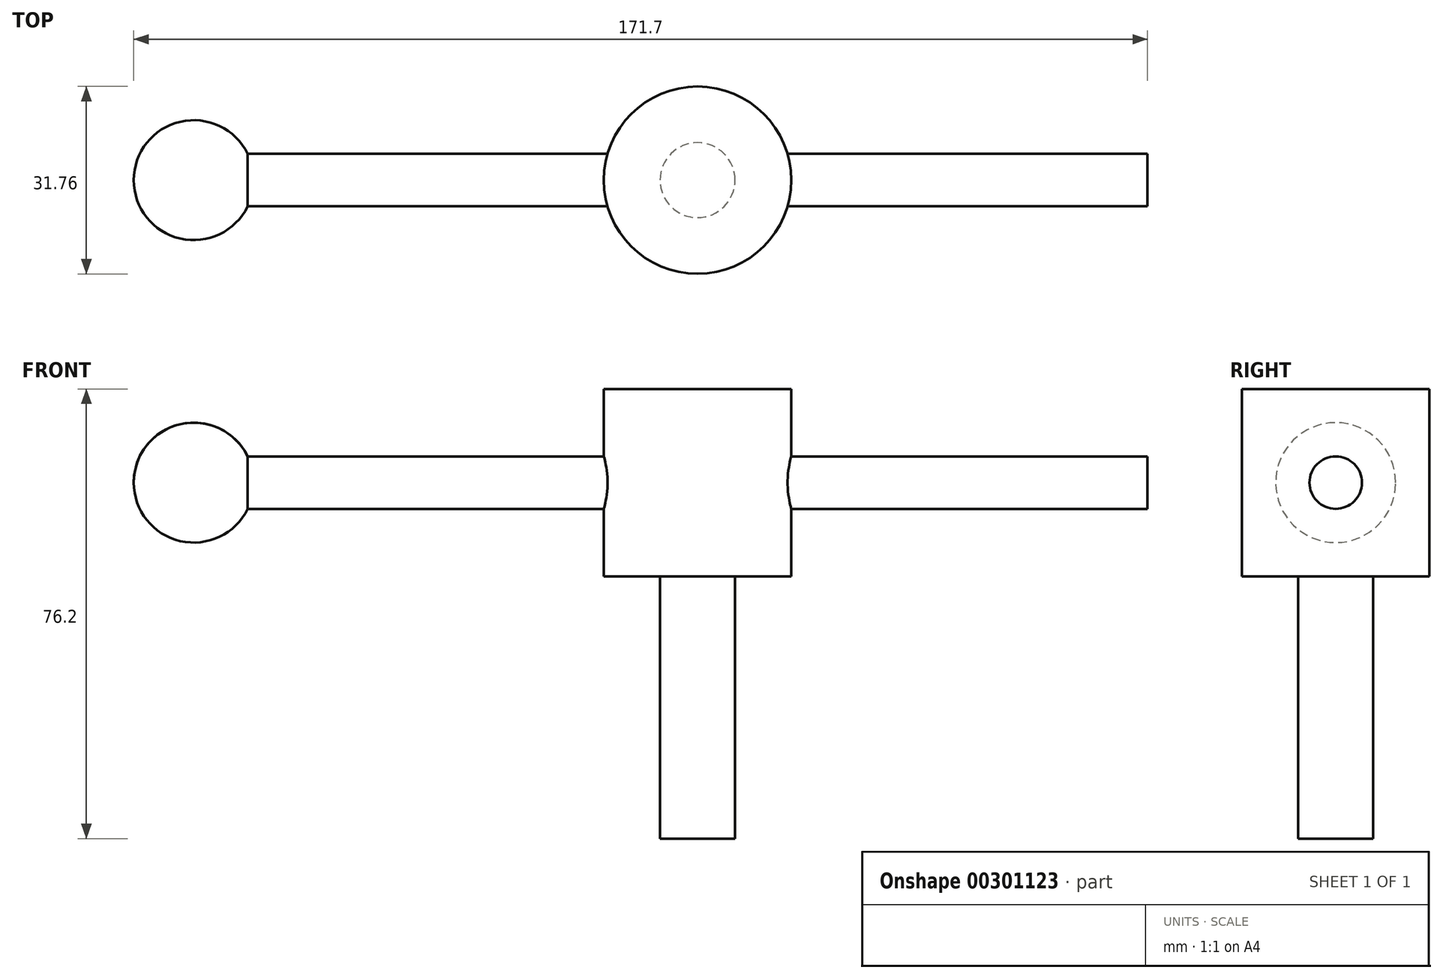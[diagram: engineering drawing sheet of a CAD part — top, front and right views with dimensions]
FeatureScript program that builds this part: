
annotation { "Feature Type Name" : "Feature", "Feature Type Description" : "" }
export const myFeature = defineFeature(function(context is Context, id is Id, definition is map)
    precondition{}
    {
        {
            var Q0;
            Q0=qCreatedBy(makeId("Top.planeOp"),FACE);
            var sketch = newSketch(context, id + "F0", { "sketchPlane" : qUnion([Q0])});
            skCircle(sketch, "E0", {"center": v(0, 0) * mm, "radius": 15.88 * mm});
            skSolve(sketch);
        }
        {
            var Q0;
            Q0 = qSketchRegion(id + "F0", true);
            extrude(context, id + "F1", {"entities" : qUnion([Q0]), "depth" : 31.75 * mm});
        }
        {
            var Q0;
            Q0=makeQuery(id+"F1.opExtrude","CAP_FACE",FACE,{"disambiguationData":[OSD([sQuery(id+"F0.wireOp",EDGE,"E0")])],"isStart":true});
            var sketch = newSketch(context, id + "F2", { "sketchPlane" : qUnion([Q0])});
            skCircle(sketch, "E1", {"center": v(0, 0) * mm, "radius": 6.35 * mm});
            skSolve(sketch);
        }
        {
            var Q0;
            Q0 = qSketchRegion(id + "F2", true);
            extrude(context, id + "F3", {"entities" : qUnion([Q0]), "operationType" : NewBodyOperationType.ADD, "depth" : 44.45 * mm});
        }
        {
            var Q0;
            Q0=qCreatedBy(makeId("Right.planeOp"),FACE);
            var sketch = newSketch(context, id + "F4", { "sketchPlane" : qUnion([Q0])});
            skLineSegment(sketch, "E2", {"start": v(0, 0) * mm, "end": v(0, 31.75) * mm});
            skPoint(sketch, "E3", {"position": v(0, 15.88) * mm});
            skCircle(sketch, "E4", {"center": v(0, 15.88) * mm, "radius": 4.45 * mm});
            skSolve(sketch);
        }
        {
            var Q0;
            Q0 = qSketchRegion(id + "F4", true);
            extrude(context, id + "F5", {"entities" : qUnion([Q0]), "operationType" : NewBodyOperationType.ADD, "depth" : 76.2 * mm, "hasSecondDirection" : true, "secondDirectionOppositeDirection" : true, "secondDirectionDepth" : 76.2 * mm});
        }
        {
            var Q0;
            Q0=qCreatedBy(makeId("Front.planeOp"),FACE);
            var sketch = newSketch(context, id + "F6", { "sketchPlane" : qUnion([Q0])});
            skLineSegment(sketch, "E5", {"start": v(0, 15.88) * mm, "end": v(-96.58, 15.88) * mm, "construction": true});
            skLineSegment(sketch, "E6", {"start": v(0, 15.88) * mm, "end": v(0, 20.32) * mm});
            skLineSegment(sketch, "E7", {"start": v(0, 15.88) * mm, "end": v(0, 11.43) * mm, "construction": true});
            skLineSegment(sketch, "E8", {"start": v(0, 20.32) * mm, "end": v(-96.26, 20.32) * mm, "construction": true});
            skLineSegment(sketch, "E9", {"start": v(0, 11.43) * mm, "end": v(-76.2, 11.43) * mm, "construction": true});
            skArc(sketch, "E10", {"start": v(-76.2, 20.32) * mm, "mid": v(-87.62, 25.78) * mm, "end": v(-95.5, 15.87) * mm});
            skLineSegment(sketch, "E11.MirrorCS", {"start": v(0, 11.43) * mm, "end": v(76.2, 11.43) * mm, "construction": true});
            skLineSegment(sketch, "E12.MirrorCS", {"start": v(0, 15.88) * mm, "end": v(96.58, 15.88) * mm, "construction": true});
            skLineSegment(sketch, "E13.MirrorCS", {"start": v(0, 20.32) * mm, "end": v(96.26, 20.32) * mm, "construction": true});
            skArc(sketch, "E14.MirrorCS", {"start": v(76.2, 20.32) * mm, "mid": v(87.62, 25.78) * mm, "end": v(95.5, 15.87) * mm});
            skLineSegment(sketch, "E15", {"start": v(95.5, 15.87) * mm, "end": v(76.2, 15.88) * mm});
            skLineSegment(sketch, "E16", {"start": v(76.2, 15.88) * mm, "end": v(76.2, 20.32) * mm});
            skLineSegment(sketch, "E17", {"start": v(-95.5, 15.87) * mm, "end": v(-76.2, 15.88) * mm});
            skLineSegment(sketch, "E18", {"start": v(-76.2, 15.88) * mm, "end": v(-76.2, 20.32) * mm});
            skSolve(sketch);
        }
        {
            var Q0;
            Q0=makeQuery(id+"F6.imprint","IMPRINT",FACE,{"disambiguationData":[TD([[makeQuery(id+"F6.imprint","IMPRINT",EDGE,{"derivedFrom":sQuery(id+"F6.wireOp",EDGE,"E14.MirrorCS")}),-1.0]])]});
            var Q1;
            Q1=makeQuery(id+"F6.imprint","IMPRINT",FACE,{"disambiguationData":[TD([[makeQuery(id+"F6.imprint","IMPRINT",EDGE,{"derivedFrom":sQuery(id+"F6.wireOp",EDGE,"E10")}),1.0]])]});
            var Q2;
            Q2=sQuery(id+"F6.wireOp",EDGE,"E12.MirrorCS");
            revolve(context, id + "F7", {"operationType" : NewBodyOperationType.ADD, "entities" : qUnion([Q0, Q1]), "axis" : qUnion([Q2]), "revolveType" : RevolveType.FULL});
        }
    });
